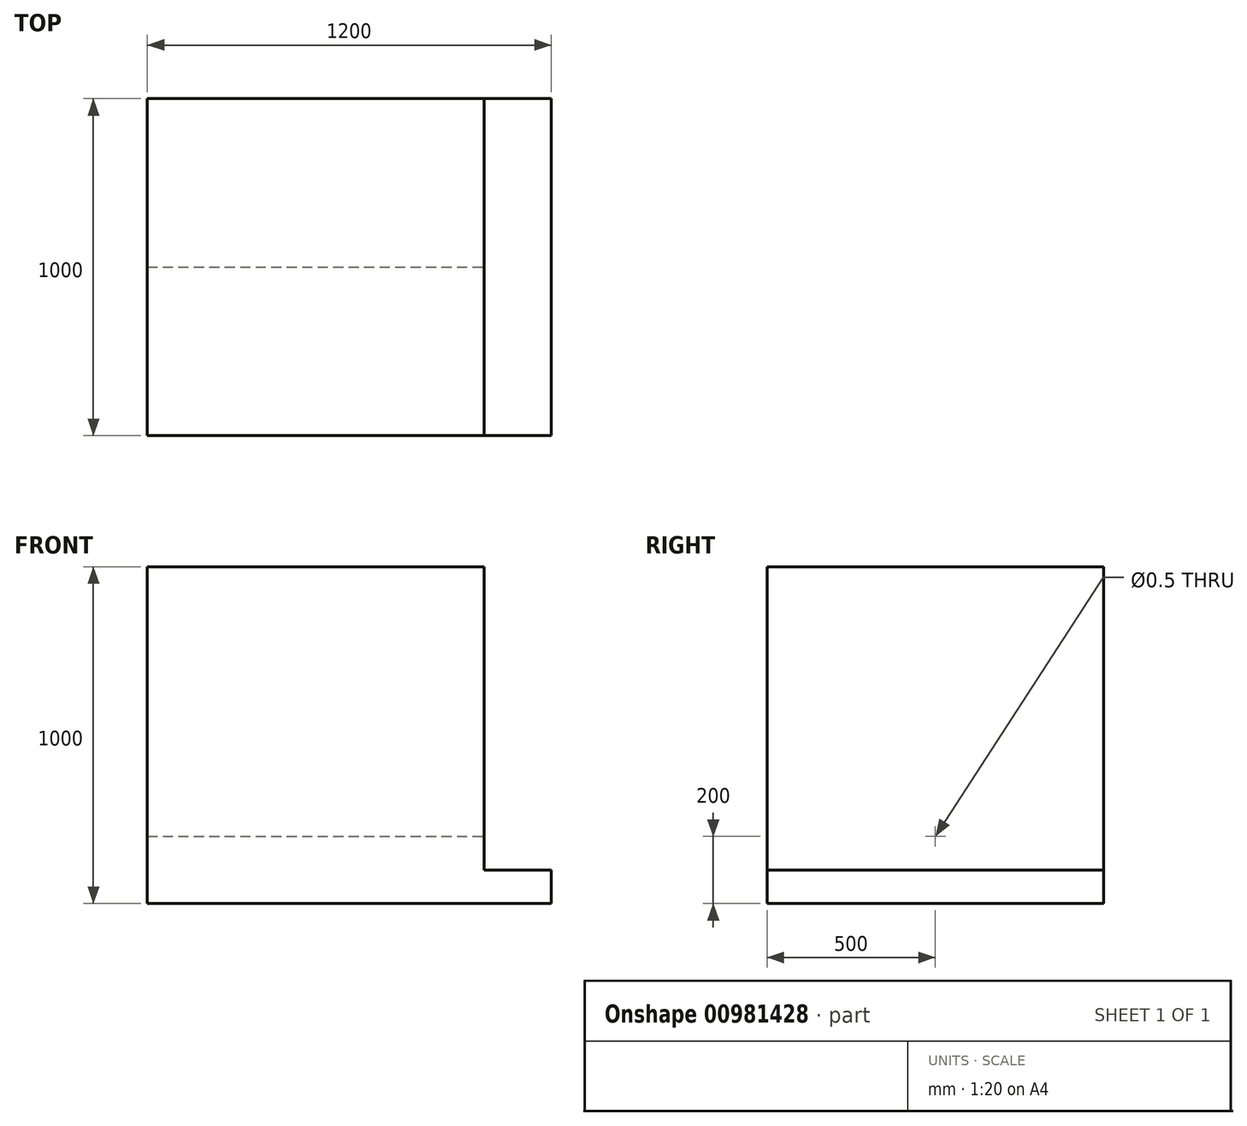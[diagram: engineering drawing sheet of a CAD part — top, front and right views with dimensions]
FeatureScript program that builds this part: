
annotation { "Feature Type Name" : "Feature", "Feature Type Description" : "" }
export const myFeature = defineFeature(function(context is Context, id is Id, definition is map)
    precondition{}
    {
        {
            var Q0;
            Q0=qCreatedBy(makeId("Front.planeOp"),FACE);
            var sketch = newSketch(context, id + "F0", { "sketchPlane" : qUnion([Q0])});
            skLineSegment(sketch, "E0.bottom", {"start": v(-600, 500) * mm, "end": v(400, 500) * mm});
            skLineSegment(sketch, "E0.top", {"start": v(-600, -500) * mm, "end": v(600, -500) * mm});
            skLineSegment(sketch, "E0.left", {"start": v(-600, 500) * mm, "end": v(-600, -500) * mm});
            skLineSegment(sketch, "E0.right", {"start": v(600, -400) * mm, "end": v(600, -500) * mm});
            skPoint(sketch, "E0.middle", {"position": v(0, 0) * mm});
            skLineSegment(sketch, "E1", {"start": v(400, 500) * mm, "end": v(400, -400) * mm});
            skLineSegment(sketch, "E2", {"start": v(400, -400) * mm, "end": v(600, -400) * mm});
            skSolve(sketch);
        }
        {
            var Q0;
            Q0 = qSketchRegion(id + "F0", true);
            extrude(context, id + "F1", {"entities" : qUnion([Q0]), "depth" : 1000 * mm, "offsetDistance" : 25 * mm});
        }
        {
            var Q0;
            Q0=makeQuery(id+"F1.opExtrude","SWEPT_FACE",FACE,{"disambiguationData":[OSD([sQuery(id+"F0.wireOp",EDGE,"E1")])]});
            cPlane(context, id + "F2", {"entities" : qUnion([Q0]), "cplaneType" : CPlaneType.OFFSET, "offset" : 0 * mm, "width" : 150 * mm, "height" : 150 * mm});
        }
        {
            var Q0;
            Q0=qCreatedBy(id+"F2.planeOp",FACE);
            var sketch = newSketch(context, id + "F3", { "sketchPlane" : qUnion([Q0])});
            skPoint(sketch, "E3", {"position": v(-500, -300) * mm});
            skSolve(sketch);
        }
        {
            var Q0;
            Q0=sQuery(id+"F3.wireOp",VERTEX,"E3");
            var Q1;
            Q1=makeQuery(id+"F1.opExtrude","SWEPT_BODY",BODY,{"disambiguationData":[OSD([sQuery(id+"F0.wireOp",EDGE,"E0.bottom"),sQuery(id+"F0.wireOp",EDGE,"E0.top"),sQuery(id+"F0.wireOp",EDGE,"E0.left"),sQuery(id+"F0.wireOp",EDGE,"E0.right"),sQuery(id+"F0.wireOp",EDGE,"E1"),sQuery(id+"F0.wireOp",EDGE,"E2")])]});
            hole(context, id + "F4", {"style" : HoleStyle.SIMPLE, "endStyle" : HoleEndStyle.THROUGH, "holeDiameter" : 0.5 * mm, "majorDiameter" : 5 * mm, "isTappedThrough" : true, "tappedDepth" : 12 * mm, "tapClearance" : 3, "startFromSketch" : true, "locations" : qUnion([Q0]), "scope" : qUnion([Q1])});
        }
    });
